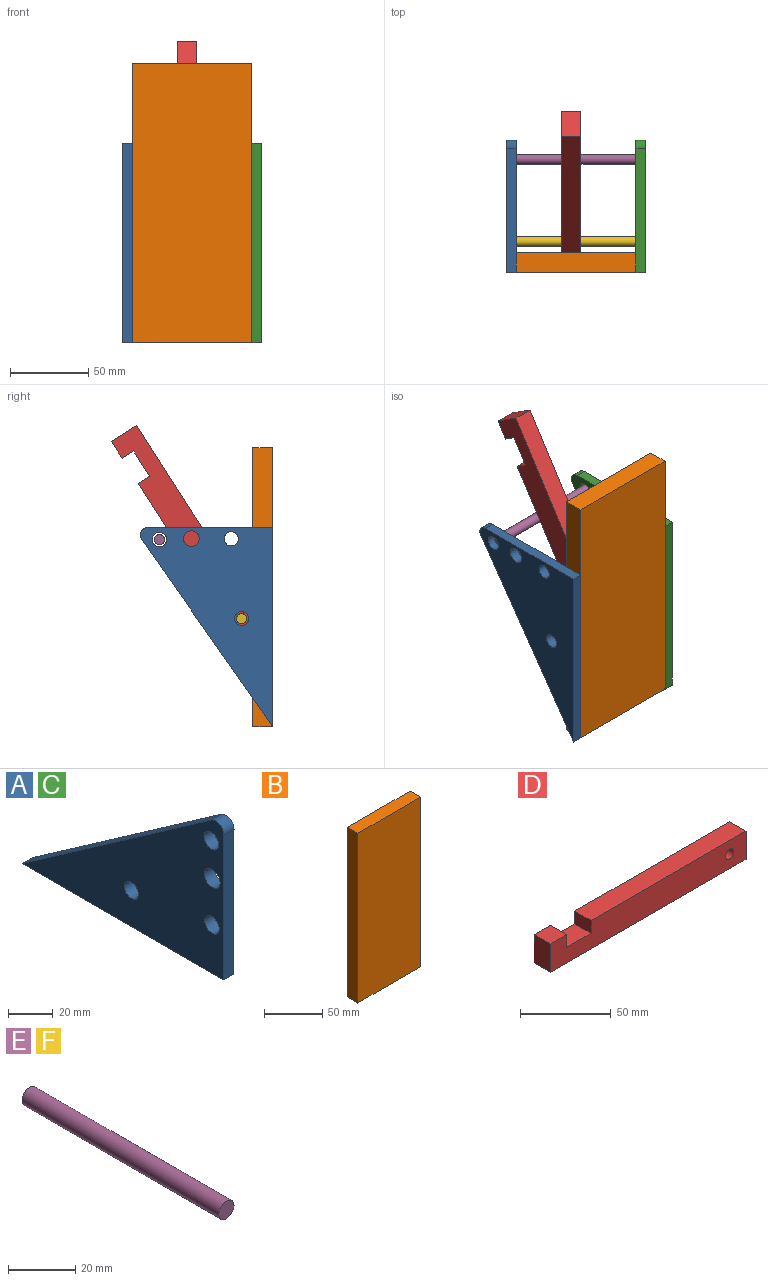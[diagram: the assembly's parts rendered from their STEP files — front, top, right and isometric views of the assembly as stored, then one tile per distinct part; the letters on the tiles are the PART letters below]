
ASSEMBLY  parts=6 mates=5
PART A: 10 faces, bbox 6.4x127.1x84.2 mm
  f0: plane 119.12x83.3mm, normal (0,0.57,0.82), area 923mm2, adj f1,f6,f8,f9
  f1: cylinder r=5.08mm len=7.99mm, axis (-1,0,0), area 70.4mm2, adj f0,f2,f8,f9
  f2: plane 79.13x6.35mm, normal (0,-1,0), area 502.5mm2, adj f1,f6,f8,f9
  f3: cylinder r=4.54mm len=9.09mm, axis (-1,0,0), area 181.3mm2, adj f8,f9
  f4: cylinder r=4.96mm len=9.92mm, axis (-1,0,0), area 197.9mm2, adj f8,f9
  f5: cylinder r=4.61mm len=9.23mm, axis (-1,0,0), area 184mm2, adj f8,f9
  f6: plane 127x6.35mm, normal (0,0,-1), area 806.5mm2, adj f0,f2,f8,f9
  f7: cylinder r=4.43mm len=8.85mm, axis (-1,0,0), area 176.6mm2, adj f8,f9
  f8: plane 127.11x84.22mm, normal (1,0,0), area 5353.1mm2, adj f0,f1,f2,f3,f4,f5,f6,f7
  f9: plane 127.11x84.22mm, normal (-1,0,0), area 5353.1mm2, adj f0,f1,f2,f3,f4,f5,f6,f7
PART B: 6 faces, bbox 76.2x12.7x177.8 mm
  f0: plane 76.2x12.7mm, normal (0,0,-1), area 967.7mm2, adj f1,f3,f4,f5
  f1: plane 177.8x12.7mm, normal (1,0,0), area 2258.1mm2, adj f0,f2,f4,f5
  f2: plane 76.2x12.7mm, normal (0,0,1), area 967.7mm2, adj f1,f3,f4,f5
  f3: plane 177.8x12.7mm, normal (-1,0,0), area 2258.1mm2, adj f0,f2,f4,f5
  f4: plane 177.8x76.2mm, normal (0,-1,0), area 13548.4mm2, adj f0,f1,f2,f3
  f5: plane 177.8x76.2mm, normal (0,1,0), area 13548.4mm2, adj f0,f1,f2,f3
PART C: same geometry as A
PART D: 11 faces, bbox 152.4x12.7x19.1 mm
  f0: plane 12.7x8.63mm, normal (1,0,0), area 109.6mm2, adj f1,f7,f9,f10
  f1: plane 12.7x12.7mm, normal (0,0,1), area 161.3mm2, adj f0,f2,f9,f10
  f2: plane 19.05x12.7mm, normal (-1,0,0), area 241.9mm2, adj f1,f3,f9,f10
  f3: plane 152.4x12.7mm, normal (0,0,-1), area 1935.5mm2, adj f2,f4,f9,f10
  f4: plane 19.05x12.7mm, normal (1,0,0), area 241.9mm2, adj f3,f5,f9,f10
  f5: plane 120.65x12.7mm, normal (0,0,1), area 1532.3mm2, adj f4,f6,f9,f10
  f6: plane 12.7x8.63mm, normal (-1,0,0), area 109.6mm2, adj f5,f7,f9,f10
  f7: plane 19.05x12.7mm, normal (0,0,1), area 241.9mm2, adj f0,f6,f9,f10
  f8: cylinder r=3.2mm len=12.7mm, axis (0,1,0), area 255.4mm2, adj f9,f10
  f9: plane 152.4x19.05mm, normal (0,-1,0), area 2706.6mm2, adj f0,f1,f2,f3,f4,f5,f6,f7
  f10: plane 152.4x19.05mm, normal (0,1,0), area 2706.6mm2, adj f0,f1,f2,f3,f4,f5,f6,f7
PART E: 3 faces, bbox 6.4x82.6x6.4 mm
  f0: plane 6.35x6.35mm, normal (0,-1,0), area 31.7mm2, adj f1
  f1: cylinder r=3.17mm len=82.55mm, axis (0,1,0), area 1646.8mm2, adj f0,f2
  f2: plane 6.35x6.35mm, normal (0,1,0), area 31.7mm2, adj f1
PART F: same geometry as E
PLACE A rot(axis=(-1,0,0),90deg) t=(-49.46,31.65,29.77)mm
PLACE B at identity fixed
PLACE C rot(axis=(-1,0,0),90deg) t=(33.09,31.65,29.77)mm
PLACE D rot(axis=(-0.66,0.66,0.36),140.3deg) t=(-14.53,67.96,130.26)mm
PLACE E rot(axis=(0,0,1),90deg) t=(8.65,59.38,63.99)mm
PLACE F rot(axis=(0,0,-1),90deg) t=(-14.55,7.09,13.65)mm
MATE fastened C.f9 <-> B.f1  axis (-1,0,0) through (33.09,-12.7,-52.87)mm
MATE fastened F.f1 <-> C.f7  axis (1,0,0) through (39.44,7.09,15.96)mm
MATE slider E.f1 <-> C.f5  axis (-1,0,0) through (-45.34,59.38,66.29)mm
MATE revolute D.f8 <-> F.f1  axis (1,0,0) through (-1.83,7.09,15.96)mm
MATE fastened A.f8 <-> B.f3  axis (1,0,0) through (-43.11,-12.7,-52.87)mm
